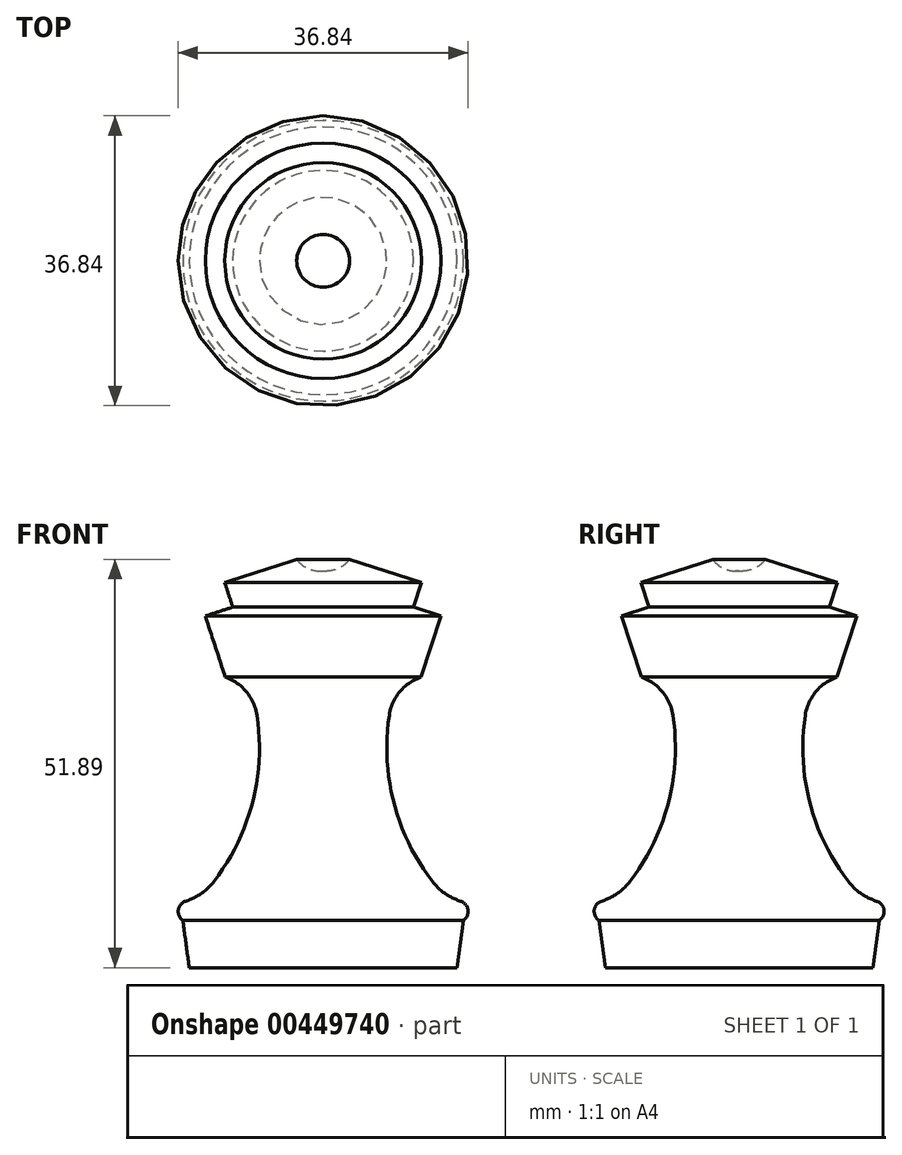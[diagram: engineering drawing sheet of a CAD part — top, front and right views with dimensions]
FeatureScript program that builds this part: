
annotation { "Feature Type Name" : "Feature", "Feature Type Description" : "" }
export const myFeature = defineFeature(function(context is Context, id is Id, definition is map)
    precondition{}
    {
        {
            var Q0;
            Q0=qCreatedBy(makeId("Front.planeOp"),FACE);
            var sketch = newSketch(context, id + "F0", { "sketchPlane" : qUnion([Q0])});
            skLineSegment(sketch, "E0", {"start": v(0, 0) * mm, "end": v(17, 0) * mm});
            skLineSegment(sketch, "E1", {"start": v(0, 0) * mm, "end": v(0, 57.42) * mm});
            skArc(sketch, "E2", {"start": v(3.35, 51.9) * mm, "mid": v(3.49, 55.76) * mm, "end": v(0, 57.42) * mm});
            skLineSegment(sketch, "E3", {"start": v(3.35, 51.9) * mm, "end": v(12.49, 48.91) * mm});
            skLineSegment(sketch, "E4", {"start": v(12.49, 48.91) * mm, "end": v(11.48, 45.82) * mm});
            skLineSegment(sketch, "E5", {"start": v(11.48, 45.82) * mm, "end": v(14.96, 44.68) * mm});
            skLineSegment(sketch, "E6", {"start": v(14.96, 44.68) * mm, "end": v(12.43, 36.92) * mm});
            skArc(sketch, "E7", {"start": v(12.43, 36.92) * mm, "mid": v(9.74, 35.06) * mm, "end": v(8.4, 32.07) * mm});
            skArc(sketch, "E8", {"start": v(8.4, 32.07) * mm, "mid": v(8.98, 20.95) * mm, "end": v(13.88, 10.96) * mm});
            skArc(sketch, "E9", {"start": v(13.88, 10.96) * mm, "mid": v(15.48, 9.43) * mm, "end": v(17.46, 8.45) * mm});
            skArc(sketch, "E10", {"start": v(17.46, 8.45) * mm, "mid": v(18.4, 7.34) * mm, "end": v(17.82, 6) * mm});
            skLineSegment(sketch, "E11", {"start": v(17.82, 6) * mm, "end": v(17, 0) * mm});
            skSolve(sketch);
        }
        {
            var Q0;
            Q0=makeQuery(id+"F0.imprint","IMPRINT",FACE,{"disambiguationData":[TD([[makeQuery(id+"F0.imprint","IMPRINT",EDGE,{"derivedFrom":sQuery(id+"F0.wireOp",EDGE,"E0")}),1.0]])]});
            var Q1;
            Q1=sQuery(id+"F0.wireOp",EDGE,"E1");
            revolve(context, id + "F1", {"entities" : qUnion([Q0]), "axis" : qUnion([Q1]), "revolveType" : RevolveType.FULL});
        }
    });
